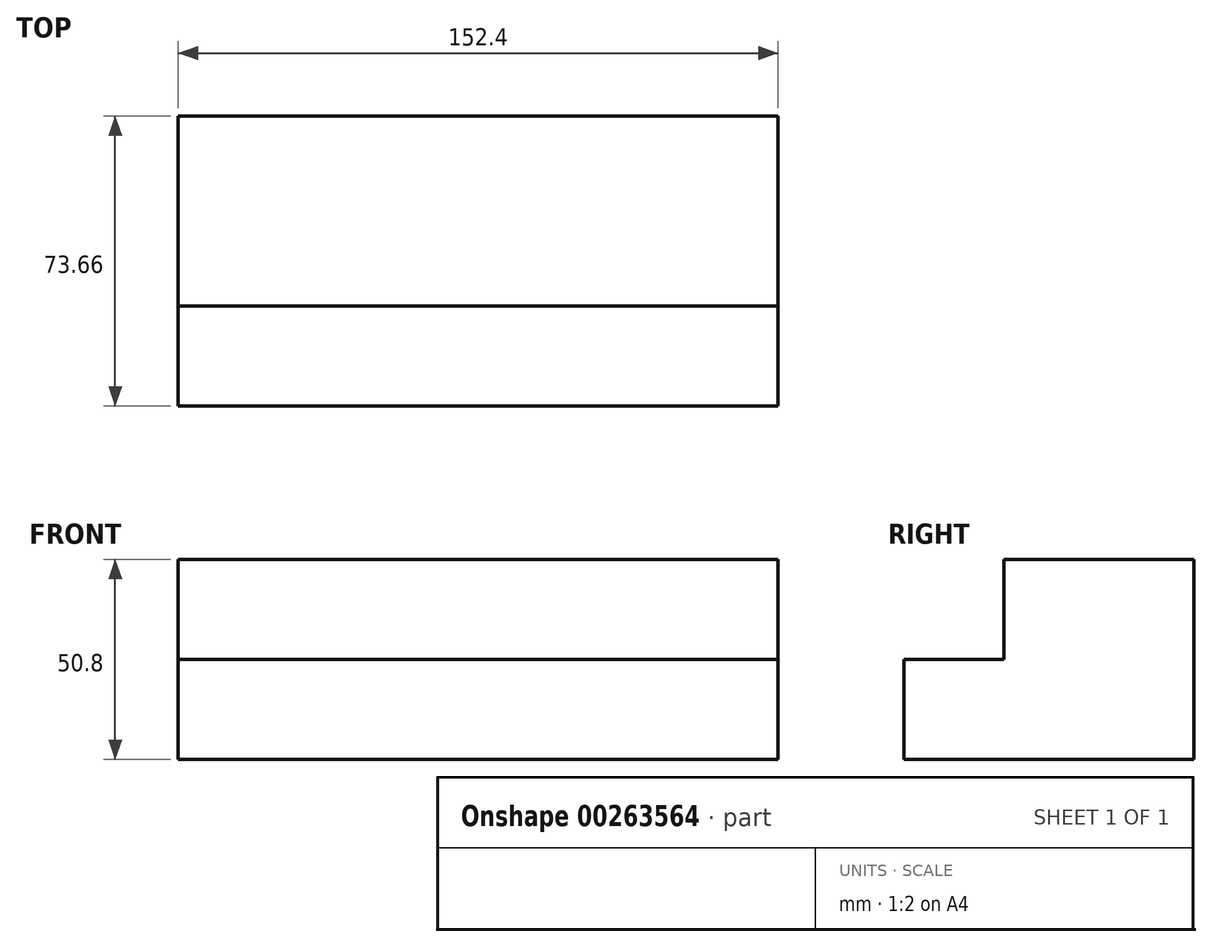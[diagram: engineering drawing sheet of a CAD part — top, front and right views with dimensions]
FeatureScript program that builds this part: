
annotation { "Feature Type Name" : "Feature", "Feature Type Description" : "" }
export const myFeature = defineFeature(function(context is Context, id is Id, definition is map)
    precondition{}
    {
        {
            var Q0;
            Q0=qCreatedBy(makeId("Front.planeOp"),FACE);
            var sketch = newSketch(context, id + "F0", { "sketchPlane" : qUnion([Q0])});
            skLineSegment(sketch, "E0", {"start": v(-76.84, 0) * mm, "end": v(75.56, 0) * mm});
            skLineSegment(sketch, "E1", {"start": v(75.56, 0) * mm, "end": v(75.56, 25.4) * mm});
            skLineSegment(sketch, "E2", {"start": v(75.56, 25.4) * mm, "end": v(-76.84, 25.4) * mm});
            skLineSegment(sketch, "E3", {"start": v(-76.84, 25.4) * mm, "end": v(-76.84, 0) * mm});
            skLineSegment(sketch, "E4", {"start": v(-76.84, 50.8) * mm, "end": v(-76.84, 25.4) * mm});
            skLineSegment(sketch, "E5", {"start": v(-76.84, 50.8) * mm, "end": v(75.56, 50.8) * mm});
            skLineSegment(sketch, "E6", {"start": v(75.56, 50.8) * mm, "end": v(75.56, 25.4) * mm});
            skSolve(sketch);
        }
        {
            var Q0;
            Q0=makeQuery(id+"F0.imprint","IMPRINT",FACE,{"disambiguationData":[TD([[makeQuery(id+"F0.imprint","IMPRINT",EDGE,{"derivedFrom":sQuery(id+"F0.wireOp",EDGE,"E2")}),-1.0]])]});
            var Q1;
            Q1=makeQuery(id+"F0.imprint","IMPRINT",FACE,{"disambiguationData":[TD([[makeQuery(id+"F0.imprint","IMPRINT",EDGE,{"derivedFrom":sQuery(id+"F0.wireOp",EDGE,"E0")}),1.0]])]});
            extrude(context, id + "F1", {"entities" : qUnion([Q0, Q1]), "depth" : 73.66 * mm});
        }
        {
            var Q0;
            Q0=makeQuery(id+"F1.opExtrude","SWEPT_FACE",FACE,{"disambiguationData":[OSD([sQuery(id+"F0.wireOp",EDGE,"E5")])]});
            var sketch = newSketch(context, id + "F2", { "sketchPlane" : qUnion([Q0])});
            skLineSegment(sketch, "E7", {"start": v(-76.84, -73.66) * mm, "end": v(-76.84, -48.26) * mm});
            skLineSegment(sketch, "E8", {"start": v(-76.84, -48.26) * mm, "end": v(75.56, -48.26) * mm});
            skLineSegment(sketch, "E9", {"start": v(75.56, -48.26) * mm, "end": v(75.56, -73.66) * mm});
            skLineSegment(sketch, "E10", {"start": v(75.56, -73.66) * mm, "end": v(-76.84, -73.66) * mm});
            skSolve(sketch);
        }
        {
            var Q0;
            Q0=makeQuery(id+"F2.imprint","IMPRINT",FACE,{"disambiguationData":[TD([[makeQuery(id+"F2.imprint","IMPRINT",EDGE,{"derivedFrom":sQuery(id+"F2.wireOp",EDGE,"E7")}),-1.0]])]});
            extrude(context, id + "F3", {"entities" : qUnion([Q0]), "operationType" : NewBodyOperationType.REMOVE, "oppositeDirection" : true, "depth" : 25.4 * mm});
        }
    });
